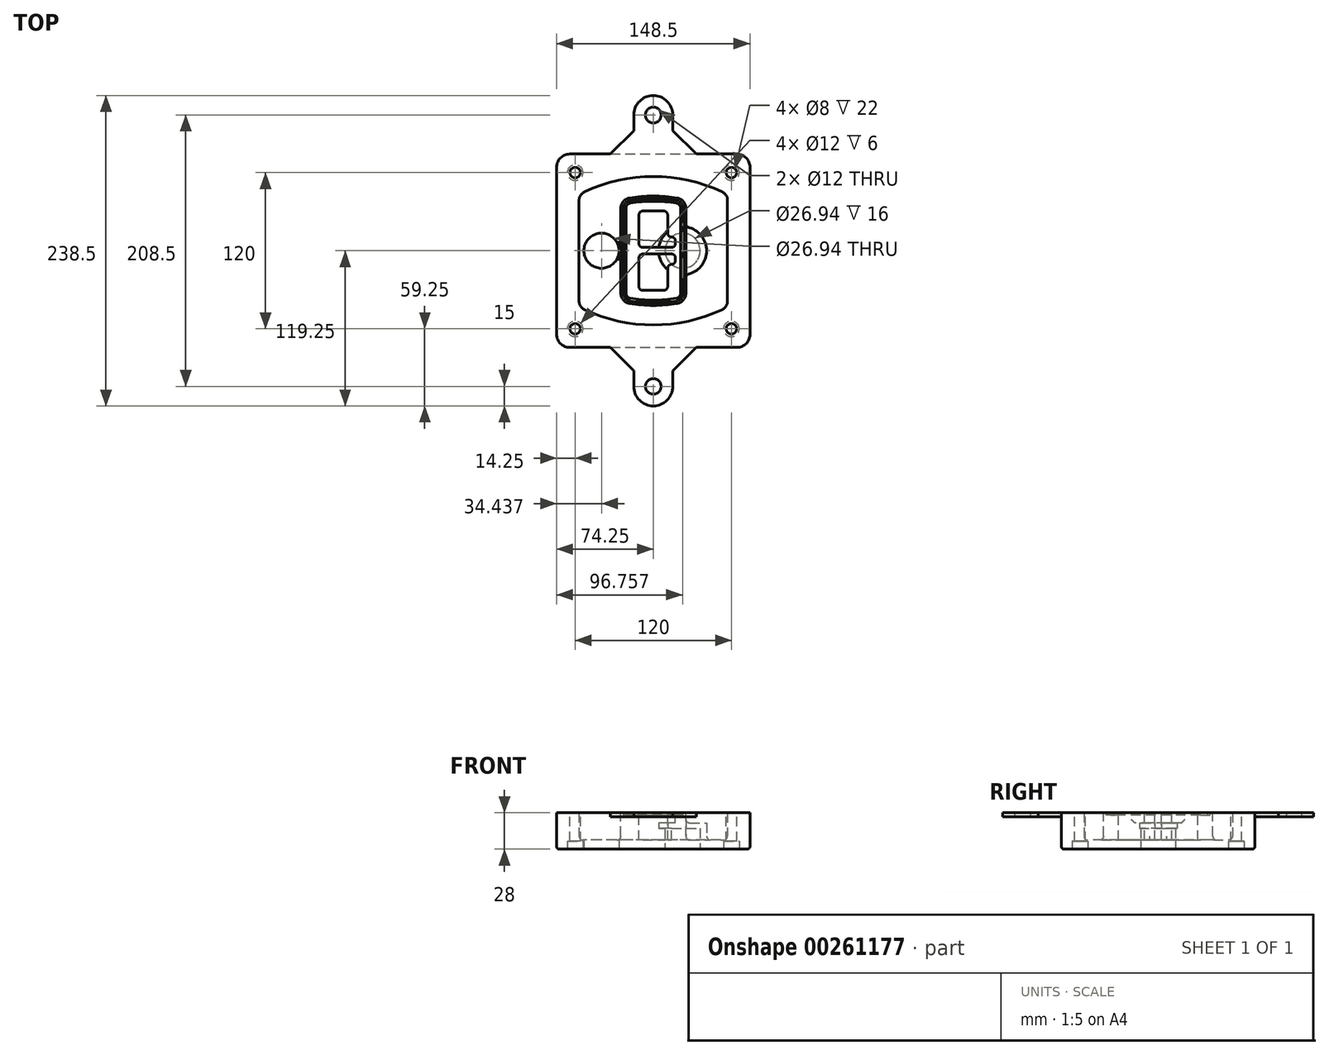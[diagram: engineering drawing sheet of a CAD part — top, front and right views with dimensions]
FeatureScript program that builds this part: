
annotation { "Feature Type Name" : "Feature", "Feature Type Description" : "" }
export const myFeature = defineFeature(function(context is Context, id is Id, definition is map)
    precondition{}
    {
        {
            var Q0;
            Q0=qCreatedBy(makeId("Top.planeOp"),FACE);
            var sketch = newSketch(context, id + "F0", { "sketchPlane" : qUnion([Q0])});
            skPoint(sketch, "E0.rect.middle", {"position": v(0, 0) * mm});
            skLineSegment(sketch, "E1.bottom", {"start": v(-64.25, -74.25) * mm, "end": v(64.25, -74.25) * mm});
            skLineSegment(sketch, "E1.top", {"start": v(-64.25, 74.25) * mm, "end": v(64.25, 74.25) * mm});
            skLineSegment(sketch, "E1.left", {"start": v(-74.25, -64.25) * mm, "end": v(-74.25, 64.25) * mm});
            skLineSegment(sketch, "E1.right", {"start": v(74.25, -64.25) * mm, "end": v(74.25, 64.25) * mm});
            skLineSegment(sketch, "E2", {"start": v(-74.25, 74.25) * mm, "end": v(74.25, -74.25) * mm, "construction": true});
            skLineSegment(sketch, "E3", {"start": v(74.25, 74.25) * mm, "end": v(-74.25, -74.25) * mm, "construction": true});
            skCircle(sketch, "E4", {"center": v(-60, 60) * mm, "radius": 4 * mm});
            skCircle(sketch, "E5", {"center": v(60, 60) * mm, "radius": 4 * mm});
            skCircle(sketch, "E6", {"center": v(60, -60) * mm, "radius": 4 * mm});
            skCircle(sketch, "E7", {"center": v(-60, -60) * mm, "radius": 4 * mm});
            skLineSegment(sketch, "E8", {"start": v(-60, 60) * mm, "end": v(60, 60) * mm, "construction": true});
            skLineSegment(sketch, "E9", {"start": v(60, 60) * mm, "end": v(60, -60) * mm, "construction": true});
            skLineSegment(sketch, "E10", {"start": v(60, -60) * mm, "end": v(-60, -60) * mm, "construction": true});
            skLineSegment(sketch, "E11", {"start": v(-60, -60) * mm, "end": v(-60, 60) * mm, "construction": true});
            skLineSegment(sketch, "E12", {"start": v(-60, 38.83) * mm, "end": v(-60, -38.83) * mm});
            skLineSegment(sketch, "E13", {"start": v(60, 38.83) * mm, "end": v(60, -38.83) * mm});
            skArc(sketch, "E14", {"start": v(54.26, 47.88) * mm, "mid": v(0, 60) * mm, "end": v(-54.26, 47.88) * mm});
            skArc(sketch, "E15", {"start": v(-54.26, -47.88) * mm, "mid": v(0, -60) * mm, "end": v(54.26, -47.88) * mm});
            skLineSegment(sketch, "E16", {"start": v(-60, 0) * mm, "end": v(60, 0) * mm, "construction": true});
            skPoint(sketch, "E17.visualSharp", {"position": v(-60, -45) * mm});
            skArc(sketch, "E17.filletArc", {"start": v(-60, -38.83) * mm, "mid": v(-58.44, -44.2) * mm, "end": v(-54.26, -47.88) * mm});
            skPoint(sketch, "E18.visualSharp", {"position": v(-60, 45) * mm});
            skArc(sketch, "E18.filletArc", {"start": v(-54.26, 47.88) * mm, "mid": v(-58.44, 44.2) * mm, "end": v(-60, 38.83) * mm});
            skPoint(sketch, "E19.visualSharp", {"position": v(60, 45) * mm});
            skArc(sketch, "E19.filletArc", {"start": v(60, 38.83) * mm, "mid": v(58.44, 44.2) * mm, "end": v(54.26, 47.88) * mm});
            skPoint(sketch, "E20.visualSharp", {"position": v(60, -45) * mm});
            skArc(sketch, "E20.filletArc", {"start": v(54.26, -47.88) * mm, "mid": v(58.44, -44.2) * mm, "end": v(60, -38.83) * mm});
            skPoint(sketch, "E21.visualSharp", {"position": v(-74.25, 74.25) * mm});
            skArc(sketch, "E21.filletArc", {"start": v(-64.25, 74.25) * mm, "mid": v(-71.32, 71.32) * mm, "end": v(-74.25, 64.25) * mm});
            skPoint(sketch, "E22.visualSharp", {"position": v(74.25, 74.25) * mm});
            skArc(sketch, "E22.filletArc", {"start": v(74.25, 64.25) * mm, "mid": v(71.32, 71.32) * mm, "end": v(64.25, 74.25) * mm});
            skPoint(sketch, "E23.visualSharp", {"position": v(74.25, -74.25) * mm});
            skArc(sketch, "E23.filletArc", {"start": v(64.25, -74.25) * mm, "mid": v(71.32, -71.32) * mm, "end": v(74.25, -64.25) * mm});
            skPoint(sketch, "E24.visualSharp", {"position": v(-74.25, -74.25) * mm});
            skArc(sketch, "E24.filletArc", {"start": v(-74.25, -64.25) * mm, "mid": v(-71.32, -71.32) * mm, "end": v(-64.25, -74.25) * mm});
            skArc(sketch, "E25.0", {"start": v(57, 38.83) * mm, "mid": v(55.9, 42.58) * mm, "end": v(52.98, 45.17) * mm});
            skLineSegment(sketch, "E25.1", {"start": v(57, 38.83) * mm, "end": v(57, -38.83) * mm});
            skArc(sketch, "E25.2", {"start": v(52.98, -45.17) * mm, "mid": v(55.9, -42.58) * mm, "end": v(57, -38.83) * mm});
            skArc(sketch, "E25.3", {"start": v(-52.98, -45.17) * mm, "mid": v(0, -57) * mm, "end": v(52.98, -45.17) * mm});
            skArc(sketch, "E25.4", {"start": v(-57, -38.83) * mm, "mid": v(-55.9, -42.58) * mm, "end": v(-52.98, -45.17) * mm});
            skArc(sketch, "E25.5", {"start": v(52.98, 45.17) * mm, "mid": v(0, 57) * mm, "end": v(-52.98, 45.17) * mm});
            skLineSegment(sketch, "E25.6", {"start": v(-57, 38.83) * mm, "end": v(-57, -38.83) * mm});
            skArc(sketch, "E25.7", {"start": v(-52.98, 45.17) * mm, "mid": v(-55.9, 42.58) * mm, "end": v(-57, 38.83) * mm});
            skArc(sketch, "E26.0", {"start": v(-55.96, 51.5) * mm, "mid": v(-61.82, 46.33) * mm, "end": v(-64, 38.83) * mm});
            skArc(sketch, "E26.1", {"start": v(55.96, 51.5) * mm, "mid": v(0, 64) * mm, "end": v(-55.96, 51.5) * mm});
            skArc(sketch, "E26.2", {"start": v(64, 38.83) * mm, "mid": v(61.82, 46.33) * mm, "end": v(55.96, 51.5) * mm});
            skLineSegment(sketch, "E26.3", {"start": v(64, 38.83) * mm, "end": v(64, -38.83) * mm});
            skArc(sketch, "E26.4", {"start": v(55.96, -51.5) * mm, "mid": v(61.82, -46.33) * mm, "end": v(64, -38.83) * mm});
            skLineSegment(sketch, "E26.5", {"start": v(-64, 38.83) * mm, "end": v(-64, -38.83) * mm});
            skArc(sketch, "E26.6", {"start": v(-55.96, -51.5) * mm, "mid": v(0, -64) * mm, "end": v(55.96, -51.5) * mm});
            skArc(sketch, "E26.7", {"start": v(-64, -38.83) * mm, "mid": v(-61.82, -46.33) * mm, "end": v(-55.96, -51.5) * mm});
            skSolve(sketch);
        }
        {
            var Q0;
            Q0=makeQuery(id+"F0.imprint","IMPRINT",FACE,{"disambiguationData":[TD([[makeQuery(id+"F0.imprint","IMPRINT",EDGE,{"derivedFrom":sQuery(id+"F0.wireOp",EDGE,"E1.bottom")}),1.0]])]});
            var Q1;
            Q1=makeQuery(id+"F0.imprint","IMPRINT",FACE,{"disambiguationData":[TD([[makeQuery(id+"F0.imprint","IMPRINT",EDGE,{"derivedFrom":sQuery(id+"F0.wireOp",EDGE,"E12")}),1.0]])]});
            var Q2;
            Q2=makeQuery(id+"F0.imprint","IMPRINT",FACE,{"disambiguationData":[TD([[makeQuery(id+"F0.imprint","IMPRINT",EDGE,{"derivedFrom":sQuery(id+"F0.wireOp",EDGE,"E25.0")}),1.0]])]});
            var Q3;
            Q3=makeQuery(id+"F0.imprint","IMPRINT",FACE,{"disambiguationData":[TD([[makeQuery(id+"F0.imprint","IMPRINT",EDGE,{"derivedFrom":sQuery(id+"F0.wireOp",EDGE,"E12")}),-1.0]])]});
            extrude(context, id + "F1", {"entities" : qUnion([Q0, Q1, Q2, Q3]), "oppositeDirection" : true, "depth" : 25 * mm});
        }
        {
            var Q0;
            Q0=makeQuery(id+"F0.imprint","IMPRINT",FACE,{"disambiguationData":[TD([[makeQuery(id+"F0.imprint","IMPRINT",EDGE,{"derivedFrom":sQuery(id+"F0.wireOp",EDGE,"E12")}),1.0]])]});
            extrude(context, id + "F2", {"entities" : qUnion([Q0]), "operationType" : NewBodyOperationType.ADD, "depth" : 3 * mm});
        }
        {
            var Q0;
            Q0=makeQuery(id+"F0.imprint","IMPRINT",FACE,{"disambiguationData":[TD([[makeQuery(id+"F0.imprint","IMPRINT",EDGE,{"derivedFrom":sQuery(id+"F0.wireOp",EDGE,"E25.0")}),1.0]])]});
            extrude(context, id + "F3", {"entities" : qUnion([Q0]), "operationType" : NewBodyOperationType.REMOVE, "oppositeDirection" : true, "depth" : 18 * mm});
        }
        {
            var Q0;
            Q0=makeQuery(id+"F2.opExtrude","CAP_FACE",FACE,{"disambiguationData":[OSD([sQuery(id+"F0.wireOp",EDGE,"E12"),sQuery(id+"F0.wireOp",EDGE,"E13"),sQuery(id+"F0.wireOp",EDGE,"E14"),sQuery(id+"F0.wireOp",EDGE,"E15"),sQuery(id+"F0.wireOp",EDGE,"E17.filletArc"),sQuery(id+"F0.wireOp",EDGE,"E18.filletArc"),sQuery(id+"F0.wireOp",EDGE,"E19.filletArc"),sQuery(id+"F0.wireOp",EDGE,"E20.filletArc"),sQuery(id+"F0.wireOp",EDGE,"E25.0"),sQuery(id+"F0.wireOp",EDGE,"E25.1"),sQuery(id+"F0.wireOp",EDGE,"E25.2"),sQuery(id+"F0.wireOp",EDGE,"E25.3"),sQuery(id+"F0.wireOp",EDGE,"E25.4"),sQuery(id+"F0.wireOp",EDGE,"E25.5"),sQuery(id+"F0.wireOp",EDGE,"E25.6"),sQuery(id+"F0.wireOp",EDGE,"E25.7")])],"isStart":false});
            var sketch = newSketch(context, id + "F4", { "sketchPlane" : qUnion([Q0])});
            skArc(sketch, "E27.0", {"start": v(-18.34, -40.45) * mm, "mid": v(0, -42) * mm, "end": v(18.34, -40.45) * mm});
            skArc(sketch, "E28.0", {"start": v(18.34, 40.45) * mm, "mid": v(0, 42) * mm, "end": v(-18.34, 40.45) * mm});
            skLineSegment(sketch, "E29", {"start": v(-25, 32.57) * mm, "end": v(-25, -32.57) * mm});
            skLineSegment(sketch, "E30", {"start": v(25, 32.57) * mm, "end": v(25, -32.57) * mm});
            skLineSegment(sketch, "E31", {"start": v(-25, 39.1) * mm, "end": v(25, 39.1) * mm, "construction": true});
            skLineSegment(sketch, "E32", {"start": v(-25, -39.1) * mm, "end": v(25, -39.1) * mm, "construction": true});
            skPoint(sketch, "E33.visualSharp", {"position": v(-25, 39.1) * mm});
            skArc(sketch, "E33.filletArc", {"start": v(-18.34, 40.45) * mm, "mid": v(-23.11, 37.73) * mm, "end": v(-25, 32.57) * mm});
            skPoint(sketch, "E34.visualSharp", {"position": v(25, 39.1) * mm});
            skArc(sketch, "E34.filletArc", {"start": v(25, 32.57) * mm, "mid": v(23.11, 37.73) * mm, "end": v(18.34, 40.45) * mm});
            skPoint(sketch, "E35.visualSharp", {"position": v(25, -39.1) * mm});
            skArc(sketch, "E35.filletArc", {"start": v(18.34, -40.45) * mm, "mid": v(23.11, -37.73) * mm, "end": v(25, -32.57) * mm});
            skPoint(sketch, "E36.visualSharp", {"position": v(-25, -39.1) * mm});
            skArc(sketch, "E36.filletArc", {"start": v(-25, -32.57) * mm, "mid": v(-23.11, -37.73) * mm, "end": v(-18.34, -40.45) * mm});
            skArc(sketch, "E37.0", {"start": v(52.98, 45.17) * mm, "mid": v(0, 57) * mm, "end": v(-52.98, 45.17) * mm});
            skArc(sketch, "E37.1", {"start": v(-52.98, 45.17) * mm, "mid": v(-55.9, 42.58) * mm, "end": v(-57, 38.83) * mm});
            skLineSegment(sketch, "E37.2", {"start": v(-57, 38.83) * mm, "end": v(-57, -38.83) * mm});
            skArc(sketch, "E37.3", {"start": v(-57, -38.83) * mm, "mid": v(-55.9, -42.58) * mm, "end": v(-52.98, -45.17) * mm});
            skArc(sketch, "E37.4", {"start": v(-52.98, -45.17) * mm, "mid": v(0, -57) * mm, "end": v(52.98, -45.17) * mm});
            skArc(sketch, "E37.5", {"start": v(52.98, -45.17) * mm, "mid": v(55.9, -42.58) * mm, "end": v(57, -38.83) * mm});
            skLineSegment(sketch, "E37.6", {"start": v(57, 38.83) * mm, "end": v(57, -38.83) * mm});
            skArc(sketch, "E37.7", {"start": v(57, 38.83) * mm, "mid": v(55.9, 42.58) * mm, "end": v(52.98, 45.17) * mm});
            skLineSegment(sketch, "E38.0", {"start": v(23, 32.57) * mm, "end": v(23, -32.57) * mm});
            skArc(sketch, "E38.1", {"start": v(18, -38.48) * mm, "mid": v(21.58, -36.44) * mm, "end": v(23, -32.57) * mm});
            skArc(sketch, "E38.2", {"start": v(-18, -38.48) * mm, "mid": v(0, -40) * mm, "end": v(18, -38.48) * mm});
            skArc(sketch, "E38.3", {"start": v(-23, -32.57) * mm, "mid": v(-21.58, -36.44) * mm, "end": v(-18, -38.48) * mm});
            skLineSegment(sketch, "E38.4", {"start": v(-23, 32.57) * mm, "end": v(-23, -32.57) * mm});
            skArc(sketch, "E38.5", {"start": v(23, 32.57) * mm, "mid": v(21.58, 36.44) * mm, "end": v(18, 38.48) * mm});
            skArc(sketch, "E38.6", {"start": v(-18, 38.48) * mm, "mid": v(-21.58, 36.44) * mm, "end": v(-23, 32.57) * mm});
            skArc(sketch, "E38.7", {"start": v(18, 38.48) * mm, "mid": v(0, 40) * mm, "end": v(-18, 38.48) * mm});
            skArc(sketch, "E39.0", {"start": v(21, 32.57) * mm, "mid": v(20.06, 35.15) * mm, "end": v(17.67, 36.5) * mm});
            skLineSegment(sketch, "E39.1", {"start": v(21, 32.57) * mm, "end": v(21, -32.57) * mm});
            skArc(sketch, "E39.2", {"start": v(17.67, -36.5) * mm, "mid": v(20.06, -35.15) * mm, "end": v(21, -32.57) * mm});
            skArc(sketch, "E39.3", {"start": v(-17.67, -36.5) * mm, "mid": v(0, -38) * mm, "end": v(17.67, -36.5) * mm});
            skArc(sketch, "E39.4", {"start": v(-21, -32.57) * mm, "mid": v(-20.06, -35.15) * mm, "end": v(-17.67, -36.5) * mm});
            skArc(sketch, "E39.5", {"start": v(17.67, 36.5) * mm, "mid": v(0, 38) * mm, "end": v(-17.67, 36.5) * mm});
            skLineSegment(sketch, "E39.6", {"start": v(-21, 32.57) * mm, "end": v(-21, -32.57) * mm});
            skArc(sketch, "E39.7", {"start": v(-17.67, 36.5) * mm, "mid": v(-20.06, 35.15) * mm, "end": v(-21, 32.57) * mm});
            skLineSegment(sketch, "E40", {"start": v(-25, 0) * mm, "end": v(25, 0) * mm, "construction": true});
            skLineSegment(sketch, "E41", {"start": v(-11, 5.5) * mm, "end": v(-11, 27.5) * mm});
            skLineSegment(sketch, "E42", {"start": v(-8, 30.5) * mm, "end": v(8, 30.5) * mm});
            skLineSegment(sketch, "E43", {"start": v(11, 27.5) * mm, "end": v(11, 13.5) * mm});
            skLineSegment(sketch, "E44", {"start": v(14, 10.5) * mm, "end": v(14, 10.5) * mm});
            skLineSegment(sketch, "E45", {"start": v(17, 7.5) * mm, "end": v(17, 5.5) * mm});
            skLineSegment(sketch, "E46", {"start": v(14, 2.5) * mm, "end": v(-8, 2.5) * mm});
            skPoint(sketch, "E47.visualSharp", {"position": v(-11, 30.5) * mm});
            skArc(sketch, "E47.filletArc", {"start": v(-8, 30.5) * mm, "mid": v(-10.12, 29.62) * mm, "end": v(-11, 27.5) * mm});
            skPoint(sketch, "E48.visualSharp", {"position": v(11, 30.5) * mm});
            skArc(sketch, "E48.filletArc", {"start": v(11, 27.5) * mm, "mid": v(10.12, 29.62) * mm, "end": v(8, 30.5) * mm});
            skPoint(sketch, "E49.visualSharp", {"position": v(11, 10.5) * mm});
            skArc(sketch, "E49.filletArc", {"start": v(11, 13.5) * mm, "mid": v(11.88, 11.38) * mm, "end": v(14, 10.5) * mm});
            skPoint(sketch, "E50.visualSharp", {"position": v(17, 10.5) * mm});
            skArc(sketch, "E50.filletArc", {"start": v(17, 7.5) * mm, "mid": v(16.12, 9.62) * mm, "end": v(14, 10.5) * mm});
            skPoint(sketch, "E51.visualSharp", {"position": v(17, 2.5) * mm});
            skArc(sketch, "E51.filletArc", {"start": v(14, 2.5) * mm, "mid": v(16.12, 3.38) * mm, "end": v(17, 5.5) * mm});
            skPoint(sketch, "E52.visualSharp", {"position": v(-11, 2.5) * mm});
            skArc(sketch, "E52.filletArc", {"start": v(-11, 5.5) * mm, "mid": v(-10.12, 3.38) * mm, "end": v(-8, 2.5) * mm});
            skLineSegment(sketch, "E53.0.MirrorCS", {"start": v(14, -2.5) * mm, "end": v(-8, -2.5) * mm});
            skArc(sketch, "E54.0.MirrorCS", {"start": v(-11, -5.5) * mm, "mid": v(-10.12, -3.38) * mm, "end": v(-8, -2.5) * mm});
            skLineSegment(sketch, "E55.0.MirrorCS", {"start": v(-11, -5.5) * mm, "end": v(-11, -27.5) * mm});
            skArc(sketch, "E56.0.MirrorCS", {"start": v(-8, -30.5) * mm, "mid": v(-10.12, -29.62) * mm, "end": v(-11, -27.5) * mm});
            skLineSegment(sketch, "E57.0.MirrorCS", {"start": v(-8, -30.5) * mm, "end": v(8, -30.5) * mm});
            skArc(sketch, "E58.0.MirrorCS", {"start": v(11, -27.5) * mm, "mid": v(10.12, -29.62) * mm, "end": v(8, -30.5) * mm});
            skLineSegment(sketch, "E59.0.MirrorCS", {"start": v(11, -27.5) * mm, "end": v(11, -13.5) * mm});
            skArc(sketch, "E60.0.MirrorCS", {"start": v(11, -13.5) * mm, "mid": v(11.88, -11.38) * mm, "end": v(14, -10.5) * mm});
            skArc(sketch, "E61.0.MirrorCS", {"start": v(17, -7.5) * mm, "mid": v(16.12, -9.62) * mm, "end": v(14, -10.5) * mm});
            skLineSegment(sketch, "E62.0.MirrorCS", {"start": v(17, -7.5) * mm, "end": v(17, -5.5) * mm});
            skArc(sketch, "E63.0.MirrorCS", {"start": v(14, -2.5) * mm, "mid": v(16.12, -3.38) * mm, "end": v(17, -5.5) * mm});
            skSolve(sketch);
        }
        {
            var Q0;
            Q0=makeQuery(id+"F4.imprint","IMPRINT",FACE,{"disambiguationData":[TD([[makeQuery(id+"F4.imprint","IMPRINT",EDGE,{"derivedFrom":sQuery(id+"F4.wireOp",EDGE,"E27.0")}),1.0]])]});
            var Q1;
            Q1=makeQuery(id+"F4.imprint","IMPRINT",FACE,{"disambiguationData":[TD([[makeQuery(id+"F4.imprint","IMPRINT",EDGE,{"derivedFrom":sQuery(id+"F4.wireOp",EDGE,"E38.0")}),-1.0]])]});
            var Q2;
            Q2=makeQuery(id+"F4.imprint","IMPRINT",FACE,{"disambiguationData":[TD([[makeQuery(id+"F4.imprint","IMPRINT",EDGE,{"derivedFrom":sQuery(id+"F4.wireOp",EDGE,"E39.0")}),1.0]])]});
            extrude(context, id + "F5", {"entities" : qUnion([Q0, Q1, Q2]), "operationType" : NewBodyOperationType.ADD, "endBound" : BoundingType.UP_TO_NEXT, "oppositeDirection" : true, "depth" : 25 * mm});
        }
        {
            var Q0;
            Q0=makeQuery(id+"F4.imprint","IMPRINT",FACE,{"disambiguationData":[TD([[makeQuery(id+"F4.imprint","IMPRINT",EDGE,{"derivedFrom":sQuery(id+"F4.wireOp",EDGE,"E38.0")}),-1.0]])]});
            extrude(context, id + "F6", {"entities" : qUnion([Q0]), "operationType" : NewBodyOperationType.REMOVE, "oppositeDirection" : true, "depth" : 2 * mm});
        }
        {
            var Q0;
            Q0=makeQuery(id+"F1.opExtrude","CAP_FACE",FACE,{"disambiguationData":[OSD([sQuery(id+"F0.wireOp",EDGE,"E1.bottom"),sQuery(id+"F0.wireOp",EDGE,"E1.top"),sQuery(id+"F0.wireOp",EDGE,"E1.left"),sQuery(id+"F0.wireOp",EDGE,"E1.right"),sQuery(id+"F0.wireOp",EDGE,"E4"),sQuery(id+"F0.wireOp",EDGE,"E5"),sQuery(id+"F0.wireOp",EDGE,"E6"),sQuery(id+"F0.wireOp",EDGE,"E7"),sQuery(id+"F0.wireOp",EDGE,"E21.filletArc"),sQuery(id+"F0.wireOp",EDGE,"E22.filletArc"),sQuery(id+"F0.wireOp",EDGE,"E23.filletArc"),sQuery(id+"F0.wireOp",EDGE,"E24.filletArc")])],"isStart":false});
            var sketch = newSketch(context, id + "F7", { "sketchPlane" : qUnion([Q0])});
            skCircle(sketch, "E64", {"center": v(22.5, 0) * mm, "radius": 13.47 * mm});
            skCircle(sketch, "E65", {"center": v(-39.81, 0) * mm, "radius": 13.47 * mm});
            skLineSegment(sketch, "E66", {"start": v(74.25, 0) * mm, "end": v(-74.25, 0) * mm});
            skCircle(sketch, "E67", {"center": v(22.5, 0) * mm, "radius": 18.47 * mm});
            skCircle(sketch, "E68", {"center": v(60, -60) * mm, "radius": 6 * mm});
            skCircle(sketch, "E69", {"center": v(-60, -60) * mm, "radius": 6 * mm});
            skCircle(sketch, "E70", {"center": v(-60, 60) * mm, "radius": 6 * mm});
            skCircle(sketch, "E71", {"center": v(60, 60) * mm, "radius": 6 * mm});
            skSolve(sketch);
        }
        {
            var Q0;
            {var subQ1=sQuery(id+"F7.wireOp",EDGE,"E66");var subQ4=sQuery(id+"F7.wireOp",EDGE,"E64");var subQ6=makeQuery(id+"F7.imprint","INTERSECT",VERTEX,{"disambiguationData":[OD(0.0)],"derivedFrom":[subQ4,subQ1]});Q0=makeQuery(id+"F7.imprint","IMPRINT",FACE,{"disambiguationData":[TD([[makeQuery(id+"F7.imprint","IMPRINT",EDGE,{"disambiguationData":[TD([[subQ6,-1.0]])],"derivedFrom":subQ4}),-1.0]])]});}
            var Q1;
            {var subQ0=sQuery(id+"F7.wireOp",EDGE,"E66");var subQ1=sQuery(id+"F7.wireOp",EDGE,"E64");var subQ3=makeQuery(id+"F7.imprint","INTERSECT",VERTEX,{"disambiguationData":[OD(0.0)],"derivedFrom":[subQ1,subQ0]});Q1=makeQuery(id+"F7.imprint","IMPRINT",FACE,{"disambiguationData":[TD([[makeQuery(id+"F7.imprint","IMPRINT",EDGE,{"disambiguationData":[TD([[subQ3,-1.0]])],"derivedFrom":subQ1}),1.0]])]});}
            var Q2;
            {var subQ0=sQuery(id+"F7.wireOp",EDGE,"E66");var subQ1=sQuery(id+"F7.wireOp",EDGE,"E64");var subQ3=makeQuery(id+"F7.imprint","INTERSECT",VERTEX,{"disambiguationData":[OD(0.0)],"derivedFrom":[subQ1,subQ0]});Q2=makeQuery(id+"F7.imprint","IMPRINT",FACE,{"disambiguationData":[TD([[makeQuery(id+"F7.imprint","IMPRINT",EDGE,{"disambiguationData":[TD([[subQ3,1.0]])],"derivedFrom":subQ1}),1.0]])]});}
            var Q3;
            {var subQ1=sQuery(id+"F7.wireOp",EDGE,"E66");var subQ4=sQuery(id+"F7.wireOp",EDGE,"E64");var subQ6=makeQuery(id+"F7.imprint","INTERSECT",VERTEX,{"disambiguationData":[OD(0.0)],"derivedFrom":[subQ4,subQ1]});Q3=makeQuery(id+"F7.imprint","IMPRINT",FACE,{"disambiguationData":[TD([[makeQuery(id+"F7.imprint","IMPRINT",EDGE,{"disambiguationData":[TD([[subQ6,1.0]])],"derivedFrom":subQ4}),-1.0]])]});}
            extrude(context, id + "F8", {"entities" : qUnion([Q0, Q1, Q2, Q3]), "operationType" : NewBodyOperationType.ADD, "oppositeDirection" : true, "depth" : 20 * mm});
        }
        {
            var Q0;
            {var subQ0=sQuery(id+"F7.wireOp",EDGE,"E66");var subQ1=sQuery(id+"F7.wireOp",EDGE,"E64");var subQ3=makeQuery(id+"F7.imprint","INTERSECT",VERTEX,{"disambiguationData":[OD(0.0)],"derivedFrom":[subQ1,subQ0]});Q0=makeQuery(id+"F7.imprint","IMPRINT",FACE,{"disambiguationData":[TD([[makeQuery(id+"F7.imprint","IMPRINT",EDGE,{"disambiguationData":[TD([[subQ3,-1.0]])],"derivedFrom":subQ1}),1.0]])]});}
            var Q1;
            {var subQ0=sQuery(id+"F7.wireOp",EDGE,"E66");var subQ1=sQuery(id+"F7.wireOp",EDGE,"E64");var subQ3=makeQuery(id+"F7.imprint","INTERSECT",VERTEX,{"disambiguationData":[OD(0.0)],"derivedFrom":[subQ1,subQ0]});Q1=makeQuery(id+"F7.imprint","IMPRINT",FACE,{"disambiguationData":[TD([[makeQuery(id+"F7.imprint","IMPRINT",EDGE,{"disambiguationData":[TD([[subQ3,1.0]])],"derivedFrom":subQ1}),1.0]])]});}
            extrude(context, id + "F9", {"entities" : qUnion([Q0, Q1]), "operationType" : NewBodyOperationType.REMOVE, "oppositeDirection" : true, "depth" : 16 * mm});
        }
        {
            var Q0;
            {var subQ0=sQuery(id+"F7.wireOp",EDGE,"E66");var subQ1=sQuery(id+"F7.wireOp",EDGE,"E65");var subQ3=makeQuery(id+"F7.imprint","INTERSECT",VERTEX,{"disambiguationData":[OD(0.0)],"derivedFrom":[subQ1,subQ0]});Q0=makeQuery(id+"F7.imprint","IMPRINT",FACE,{"disambiguationData":[TD([[makeQuery(id+"F7.imprint","IMPRINT",EDGE,{"disambiguationData":[TD([[subQ3,-1.0]])],"derivedFrom":subQ1}),1.0]])]});}
            var Q1;
            {var subQ0=sQuery(id+"F7.wireOp",EDGE,"E66");var subQ1=sQuery(id+"F7.wireOp",EDGE,"E65");var subQ3=makeQuery(id+"F7.imprint","INTERSECT",VERTEX,{"disambiguationData":[OD(0.0)],"derivedFrom":[subQ1,subQ0]});Q1=makeQuery(id+"F7.imprint","IMPRINT",FACE,{"disambiguationData":[TD([[makeQuery(id+"F7.imprint","IMPRINT",EDGE,{"disambiguationData":[TD([[subQ3,1.0]])],"derivedFrom":subQ1}),1.0]])]});}
            extrude(context, id + "F10", {"entities" : qUnion([Q0, Q1]), "operationType" : NewBodyOperationType.REMOVE, "oppositeDirection" : true, "depth" : 25 * mm});
        }
        {
            var Q0;
            Q0=makeQuery(id+"F7.imprint","IMPRINT",FACE,{"disambiguationData":[TD([[makeQuery(id+"F7.imprint","IMPRINT",EDGE,{"derivedFrom":sQuery(id+"F7.wireOp",EDGE,"E68")}),1.0]])]});
            var Q1;
            Q1=makeQuery(id+"F7.imprint","IMPRINT",FACE,{"disambiguationData":[TD([[makeQuery(id+"F7.imprint","IMPRINT",EDGE,{"derivedFrom":makeQuery(id+"F1.opExtrude","CAP_EDGE",EDGE,{"disambiguationData":[OSD([sQuery(id+"F0.wireOp",EDGE,"E5")])],"isStart":false})}),-1.0]])]});
            var Q2;
            Q2=makeQuery(id+"F7.imprint","IMPRINT",FACE,{"disambiguationData":[TD([[makeQuery(id+"F7.imprint","IMPRINT",EDGE,{"derivedFrom":sQuery(id+"F7.wireOp",EDGE,"E69")}),1.0]])]});
            var Q3;
            Q3=makeQuery(id+"F7.imprint","IMPRINT",FACE,{"disambiguationData":[TD([[makeQuery(id+"F7.imprint","IMPRINT",EDGE,{"derivedFrom":makeQuery(id+"F1.opExtrude","CAP_EDGE",EDGE,{"disambiguationData":[OSD([sQuery(id+"F0.wireOp",EDGE,"E4")])],"isStart":false})}),-1.0]])]});
            var Q4;
            Q4=makeQuery(id+"F7.imprint","IMPRINT",FACE,{"disambiguationData":[TD([[makeQuery(id+"F7.imprint","IMPRINT",EDGE,{"derivedFrom":sQuery(id+"F7.wireOp",EDGE,"E70")}),1.0]])]});
            var Q5;
            Q5=makeQuery(id+"F7.imprint","IMPRINT",FACE,{"disambiguationData":[TD([[makeQuery(id+"F7.imprint","IMPRINT",EDGE,{"derivedFrom":makeQuery(id+"F1.opExtrude","CAP_EDGE",EDGE,{"disambiguationData":[OSD([sQuery(id+"F0.wireOp",EDGE,"E7")])],"isStart":false})}),-1.0]])]});
            var Q6;
            Q6=makeQuery(id+"F7.imprint","IMPRINT",FACE,{"disambiguationData":[TD([[makeQuery(id+"F7.imprint","IMPRINT",EDGE,{"derivedFrom":sQuery(id+"F7.wireOp",EDGE,"E71")}),1.0]])]});
            var Q7;
            Q7=makeQuery(id+"F7.imprint","IMPRINT",FACE,{"disambiguationData":[TD([[makeQuery(id+"F7.imprint","IMPRINT",EDGE,{"derivedFrom":makeQuery(id+"F1.opExtrude","CAP_EDGE",EDGE,{"disambiguationData":[OSD([sQuery(id+"F0.wireOp",EDGE,"E6")])],"isStart":false})}),-1.0]])]});
            extrude(context, id + "F11", {"entities" : qUnion([Q0, Q1, Q2, Q3, Q4, Q5, Q6, Q7]), "operationType" : NewBodyOperationType.REMOVE, "oppositeDirection" : true, "depth" : 6 * mm});
        }
        {
            var Q0;
            Q0=makeQuery(id+"F9.boolean.opBoolean","COPY",FACE,{"derivedFrom":makeQuery(id+"F9.opExtrude","CAP_FACE",FACE,{"disambiguationData":[OSD([sQuery(id+"F7.wireOp",EDGE,"E64")])],"isStart":false})});
            var sketch = newSketch(context, id + "F12", { "sketchPlane" : qUnion([Q0])});
            skArc(sketch, "E72.0", {"start": v(11, 14.45) * mm, "mid": v(6.45, 9.13) * mm, "end": v(4.2, 2.5) * mm});
            skArc(sketch, "E72.1", {"start": v(4.2, -2.5) * mm, "mid": v(6.45, -9.13) * mm, "end": v(11, -14.45) * mm});
            skLineSegment(sketch, "E73", {"start": v(4.2, -2.5) * mm, "end": v(14, -2.5) * mm});
            skLineSegment(sketch, "E74.0", {"start": v(14, 2.5) * mm, "end": v(4.2, 2.5) * mm});
            skArc(sketch, "E74.1", {"start": v(14, 2.5) * mm, "mid": v(16.12, 3.38) * mm, "end": v(17, 5.5) * mm});
            skLineSegment(sketch, "E74.2", {"start": v(17, 7.5) * mm, "end": v(17, 5.5) * mm});
            skArc(sketch, "E74.3", {"start": v(17, 7.5) * mm, "mid": v(16.12, 9.62) * mm, "end": v(14, 10.5) * mm});
            skArc(sketch, "E74.4", {"start": v(11, 13.5) * mm, "mid": v(11.88, 11.38) * mm, "end": v(14, 10.5) * mm});
            skLineSegment(sketch, "E74.5", {"start": v(11, 14.45) * mm, "end": v(11, 13.5) * mm});
            skLineSegment(sketch, "E74.7", {"start": v(14, -2.5) * mm, "end": v(4.2, -2.5) * mm});
            skArc(sketch, "E74.8", {"start": v(14, -2.5) * mm, "mid": v(16.12, -3.38) * mm, "end": v(17, -5.5) * mm});
            skLineSegment(sketch, "E74.9", {"start": v(17, -7.5) * mm, "end": v(17, -5.5) * mm});
            skArc(sketch, "E74.10", {"start": v(17, -7.5) * mm, "mid": v(16.12, -9.62) * mm, "end": v(14, -10.5) * mm});
            skArc(sketch, "E74.11", {"start": v(11, -13.5) * mm, "mid": v(11.88, -11.38) * mm, "end": v(14, -10.5) * mm});
            skLineSegment(sketch, "E74.12", {"start": v(11, -14.45) * mm, "end": v(11, -13.5) * mm});
            skPoint(sketch, "E75.orphan", {"position": v(11, -27.5) * mm});
            skPoint(sketch, "E76.orphan", {"position": v(-8, -2.5) * mm});
            skPoint(sketch, "E77.orphan", {"position": v(-8, 2.5) * mm});
            skPoint(sketch, "E78.orphan", {"position": v(11, 27.5) * mm});
            skSolve(sketch);
        }
        {
            var Q0;
            {var subQ7=sQuery(id+"F12.wireOp",EDGE,"E72.0");var subQ14=sQuery(id+"F12.wireOp",EDGE,"E72.1");var subQ16=sQuery(id+"F12.wireOp",EDGE,"E74.1");var subQ18=sQuery(id+"F12.wireOp",EDGE,"E74.8");Q0=qUnion([makeQuery(id+"F12.imprint","IMPRINT",FACE,{"disambiguationData":[TD([[makeQuery(id+"F12.imprint","IMPRINT",EDGE,{"derivedFrom":subQ7}),1.0]])]}),makeQuery(id+"F12.imprint","IMPRINT",FACE,{"disambiguationData":[TD([[makeQuery(id+"F12.imprint","IMPRINT",EDGE,{"derivedFrom":subQ14}),1.0]])]}),makeQuery(id+"F12.imprint","IMPRINT",FACE,{"disambiguationData":[TD([[makeQuery(id+"F12.imprint","IMPRINT",EDGE,{"derivedFrom":subQ16}),1.0]])]}),makeQuery(id+"F12.imprint","IMPRINT",FACE,{"disambiguationData":[TD([[makeQuery(id+"F12.imprint","IMPRINT",EDGE,{"derivedFrom":subQ18}),-1.0]])]})]);}
            var Q1;
            Q1=makeQuery(id+"F5.boolean.opBoolean","SPLIT",FACE,{"disambiguationData":[TD([makeQuery(id+"F5.opExtrude","SWEPT_FACE",FACE,{"disambiguationData":[OSD([sQuery(id+"F4.wireOp",EDGE,"E41")])]})])],"derivedFrom":makeQuery(id+"F3.boolean.opBoolean","COPY",FACE,{"derivedFrom":makeQuery(id+"F3.opExtrude","CAP_FACE",FACE,{"disambiguationData":[OSD([sQuery(id+"F0.wireOp",EDGE,"E25.0"),sQuery(id+"F0.wireOp",EDGE,"E25.1"),sQuery(id+"F0.wireOp",EDGE,"E25.2"),sQuery(id+"F0.wireOp",EDGE,"E25.3"),sQuery(id+"F0.wireOp",EDGE,"E25.4"),sQuery(id+"F0.wireOp",EDGE,"E25.5"),sQuery(id+"F0.wireOp",EDGE,"E25.6"),sQuery(id+"F0.wireOp",EDGE,"E25.7")])],"isStart":false})})});
            extrude(context, id + "F13", {"entities" : qUnion([Q0]), "operationType" : NewBodyOperationType.REMOVE, "endBound" : BoundingType.UP_TO_SURFACE, "endBoundEntityFace" : qUnion([Q1]), "depth" : 25 * mm});
        }
        {
            var Q0;
            Q0=makeQuery(id+"F3.boolean.opBoolean","COPY",EDGE,{"derivedFrom":makeQuery(id+"F3.opExtrude","CAP_EDGE",EDGE,{"disambiguationData":[OSD([sQuery(id+"F0.wireOp",EDGE,"E25.6")])],"isStart":false})});
            var Q1;
            Q1=makeQuery(id+"F8.boolean.opBoolean","INTERSECT",EDGE,{"derivedFrom":[makeQuery(id+"F5.opExtrude","SWEPT_FACE",FACE,{"disambiguationData":[OSD([sQuery(id+"F4.wireOp",EDGE,"E30")])]}),makeQuery(id+"F8.opExtrude","CAP_FACE",FACE,{"disambiguationData":[OSD([sQuery(id+"F7.wireOp",EDGE,"E67")])],"isStart":false})]});
            var Q2;
            Q2=makeQuery(id+"F8.boolean.opBoolean","INTERSECT",EDGE,{"disambiguationData":[OD(1.0)],"derivedFrom":[makeQuery(id+"F5.opExtrude","SWEPT_FACE",FACE,{"disambiguationData":[OSD([sQuery(id+"F4.wireOp",EDGE,"E30")])]}),makeQuery(id+"F8.opExtrude","SWEPT_FACE",FACE,{"disambiguationData":[OSD([sQuery(id+"F7.wireOp",EDGE,"E67")])]})]});
            var Q3;
            {var subQ0=sQuery(id+"F4.wireOp",EDGE,"E30");Q3=makeQuery(id+"F8.boolean.opBoolean","SPLIT",EDGE,{"disambiguationData":[TD([makeQuery(id+"F5.opExtrude","SWEPT_FACE",FACE,{"disambiguationData":[OSD([sQuery(id+"F4.wireOp",EDGE,"E35.filletArc")])]})])],"derivedFrom":makeQuery(id+"F5.opExtrude","CAP_EDGE",EDGE,{"disambiguationData":[OSD([subQ0])],"isStart":false})});}
            var Q4;
            {var subQ0=sQuery(id+"F0.wireOp",EDGE,"E25.7");var subQ1=sQuery(id+"F0.wireOp",EDGE,"E25.1");var subQ2=sQuery(id+"F0.wireOp",EDGE,"E25.6");var subQ3=sQuery(id+"F0.wireOp",EDGE,"E25.5");var subQ4=sQuery(id+"F0.wireOp",EDGE,"E25.4");var subQ5=sQuery(id+"F0.wireOp",EDGE,"E25.0");var subQ6=sQuery(id+"F0.wireOp",EDGE,"E25.2");var subQ7=sQuery(id+"F0.wireOp",EDGE,"E25.3");Q4=makeQuery(id+"F8.boolean.opBoolean","INTERSECT",EDGE,{"derivedFrom":[makeQuery(id+"F5.boolean.opBoolean","SPLIT",FACE,{"disambiguationData":[TD([makeQuery(id+"F2.opExtrude","SWEPT_FACE",FACE,{"disambiguationData":[OSD([subQ5])]})])],"derivedFrom":makeQuery(id+"F3.boolean.opBoolean","COPY",FACE,{"derivedFrom":makeQuery(id+"F3.opExtrude","CAP_FACE",FACE,{"disambiguationData":[OSD([subQ5,subQ1,subQ6,subQ7,subQ4,subQ3,subQ2,subQ0])],"isStart":false})})}),makeQuery(id+"F8.opExtrude","SWEPT_FACE",FACE,{"disambiguationData":[OSD([sQuery(id+"F7.wireOp",EDGE,"E67")])]})]});}
            var Q5;
            Q5=makeQuery(id+"F8.boolean.opBoolean","INTERSECT",EDGE,{"disambiguationData":[OD(0.0)],"derivedFrom":[makeQuery(id+"F5.opExtrude","SWEPT_FACE",FACE,{"disambiguationData":[OSD([sQuery(id+"F4.wireOp",EDGE,"E30")])]}),makeQuery(id+"F8.opExtrude","SWEPT_FACE",FACE,{"disambiguationData":[OSD([sQuery(id+"F7.wireOp",EDGE,"E67")])]})]});
            fillet(context, id + "F14", {"entities" : qUnion([Q0, Q1, Q2, Q3, Q4, Q5]), "radius" : 3 * mm, "tangentPropagation" : true, "allowEdgeOverflow" : false});
        }
        {
            var Q0;
            Q0=makeQuery(id+"F1.opExtrude","CAP_EDGE",EDGE,{"disambiguationData":[OSD([sQuery(id+"F0.wireOp",EDGE,"E1.bottom")])],"isStart":false});
            fillet(context, id + "F15", {"entities" : qUnion([Q0]), "radius" : 2 * mm, "tangentPropagation" : true, "allowEdgeOverflow" : false});
        }
        {
            var Q0;
            {var subQ0=sQuery(id+"F0.wireOp",EDGE,"E22.filletArc");var subQ1=sQuery(id+"F0.wireOp",EDGE,"E7");var subQ2=sQuery(id+"F0.wireOp",EDGE,"E6");var subQ3=sQuery(id+"F0.wireOp",EDGE,"E5");var subQ4=sQuery(id+"F0.wireOp",EDGE,"E4");var subQ5=sQuery(id+"F0.wireOp",EDGE,"E1.bottom");var subQ6=sQuery(id+"F0.wireOp",EDGE,"E21.filletArc");var subQ7=sQuery(id+"F0.wireOp",EDGE,"E1.top");var subQ8=sQuery(id+"F0.wireOp",EDGE,"E1.left");var subQ9=sQuery(id+"F0.wireOp",EDGE,"E1.right");var subQ10=sQuery(id+"F0.wireOp",EDGE,"E23.filletArc");var subQ11=sQuery(id+"F0.wireOp",EDGE,"E24.filletArc");Q0=makeQuery(id+"F2.boolean.opBoolean","SPLIT",FACE,{"disambiguationData":[TD([makeQuery(id+"F1.opExtrude","SWEPT_FACE",FACE,{"disambiguationData":[OSD([subQ5])]})])],"derivedFrom":makeQuery(id+"F1.opExtrude","CAP_FACE",FACE,{"disambiguationData":[OSD([subQ5,subQ7,subQ8,subQ9,subQ4,subQ3,subQ2,subQ1,subQ6,subQ0,subQ10,subQ11])],"isStart":true})});}
            var sketch = newSketch(context, id + "F16", { "sketchPlane" : qUnion([Q0])});
            skCircle(sketch, "E79", {"center": v(0, 104.25) * mm, "radius": 6 * mm});
            skLineSegment(sketch, "E80", {"start": v(-33, 74.25) * mm, "end": v(-15, 92.25) * mm});
            skLineSegment(sketch, "E81", {"start": v(33, 74.25) * mm, "end": v(15, 92.25) * mm});
            skLineSegment(sketch, "E82", {"start": v(-33, 74.25) * mm, "end": v(33, 74.25) * mm});
            skArc(sketch, "E83", {"start": v(-15, 104.25) * mm, "mid": v(0, 119.25) * mm, "end": v(15, 104.25) * mm});
            skLineSegment(sketch, "E84", {"start": v(-15, 104.25) * mm, "end": v(-15, 92.25) * mm});
            skLineSegment(sketch, "E85", {"start": v(15, 104.25) * mm, "end": v(15, 92.25) * mm});
            skLineSegment(sketch, "E86", {"start": v(0, 74.25) * mm, "end": v(0, 104.25) * mm, "construction": true});
            skLineSegment(sketch, "E87", {"start": v(0, 104.25) * mm, "end": v(-37.02, 104.25) * mm, "construction": true});
            skLineSegment(sketch, "E88", {"start": v(0, 104.25) * mm, "end": v(29.43, 104.25) * mm, "construction": true});
            skLineSegment(sketch, "E89", {"start": v(0, 0) * mm, "end": v(0, 159.4) * mm, "construction": true});
            skPoint(sketch, "E89.endSnap0", {"position": v(0, 119.25) * mm});
            skLineSegment(sketch, "E90", {"start": v(0, 0) * mm, "end": v(0, -130.65) * mm, "construction": true});
            skLineSegment(sketch, "E91", {"start": v(0, 0) * mm, "end": v(-126.51, 0) * mm, "construction": true});
            skPoint(sketch, "E91.endSnap0", {"position": v(-74.25, 0) * mm});
            skLineSegment(sketch, "E92", {"start": v(0, 0) * mm, "end": v(120.88, 0) * mm, "construction": true});
            skLineSegment(sketch, "E93", {"start": v(-64.25, 74.25) * mm, "end": v(64.25, 74.25) * mm});
            skLineSegment(sketch, "E94", {"start": v(74.25, 64.25) * mm, "end": v(74.25, -64.25) * mm});
            skLineSegment(sketch, "E95", {"start": v(-74.25, -64.25) * mm, "end": v(-74.25, 64.25) * mm});
            skCircle(sketch, "E96", {"center": v(-60, 60) * mm, "radius": 4 * mm});
            skArc(sketch, "E97", {"start": v(-64.25, 74.25) * mm, "mid": v(-71.32, 71.32) * mm, "end": v(-74.25, 64.25) * mm});
            skArc(sketch, "E98", {"start": v(74.25, 64.25) * mm, "mid": v(71.32, 71.32) * mm, "end": v(64.25, 74.25) * mm});
            skCircle(sketch, "E99", {"center": v(60, 60) * mm, "radius": 4 * mm});
            skLineSegment(sketch, "E100", {"start": v(-60, 0) * mm, "end": v(-60, 38.83) * mm});
            skArc(sketch, "E101", {"start": v(-54.26, 47.88) * mm, "mid": v(-58.44, 44.2) * mm, "end": v(-60, 38.83) * mm});
            skLineSegment(sketch, "E102", {"start": v(60, 0) * mm, "end": v(60, 38.83) * mm});
            skArc(sketch, "E103", {"start": v(60, 38.83) * mm, "mid": v(58.44, 44.2) * mm, "end": v(54.26, 47.88) * mm});
            skArc(sketch, "E104", {"start": v(54.26, 47.88) * mm, "mid": v(0, 59.99) * mm, "end": v(-54.26, 47.88) * mm});
            skArc(sketch, "E105.MirrorCS", {"start": v(-54.26, -47.88) * mm, "mid": v(-58.44, -44.2) * mm, "end": v(-60, -38.83) * mm});
            skArc(sketch, "E106.MirrorCS", {"start": v(60, -38.83) * mm, "mid": v(58.44, -44.2) * mm, "end": v(54.26, -47.88) * mm});
            skCircle(sketch, "E107.MirrorC", {"center": v(-60, -60) * mm, "radius": 4 * mm});
            skCircle(sketch, "E108.MirrorC", {"center": v(60, -60) * mm, "radius": 4 * mm});
            skLineSegment(sketch, "E109.MirrorCS", {"start": v(15, -104.25) * mm, "end": v(15, -92.25) * mm});
            skLineSegment(sketch, "E110.MirrorCS", {"start": v(-64.25, -74.25) * mm, "end": v(64.25, -74.25) * mm});
            skArc(sketch, "E111.MirrorCS", {"start": v(-64.25, -74.25) * mm, "mid": v(-71.32, -71.32) * mm, "end": v(-74.25, -64.25) * mm});
            skArc(sketch, "E112.MirrorCS", {"start": v(74.25, -64.25) * mm, "mid": v(71.32, -71.32) * mm, "end": v(64.25, -74.25) * mm});
            skLineSegment(sketch, "E113.MirrorCS", {"start": v(0, -74.25) * mm, "end": v(0, -104.25) * mm, "construction": true});
            skLineSegment(sketch, "E114.MirrorCS", {"start": v(33, -74.25) * mm, "end": v(15, -92.25) * mm});
            skLineSegment(sketch, "E115.MirrorCS", {"start": v(0, -104.25) * mm, "end": v(29.43, -104.25) * mm, "construction": true});
            skArc(sketch, "E116.MirrorCS", {"start": v(-15, -104.25) * mm, "mid": v(0, -119.25) * mm, "end": v(15, -104.25) * mm});
            skLineSegment(sketch, "E117.MirrorCS", {"start": v(-33, -74.25) * mm, "end": v(33, -74.25) * mm});
            skLineSegment(sketch, "E118.MirrorCS", {"start": v(-33, -74.25) * mm, "end": v(-15, -92.25) * mm});
            skCircle(sketch, "E119.MirrorC", {"center": v(0, -104.25) * mm, "radius": 6 * mm});
            skPoint(sketch, "E120.MirrorP", {"position": v(0, -119.25) * mm});
            skArc(sketch, "E121.MirrorCS", {"start": v(54.26, -47.88) * mm, "mid": v(0, -59.99) * mm, "end": v(-54.26, -47.88) * mm});
            skLineSegment(sketch, "E122.MirrorCS", {"start": v(0, -104.25) * mm, "end": v(-37.02, -104.25) * mm, "construction": true});
            skLineSegment(sketch, "E123.MirrorCS", {"start": v(-15, -104.25) * mm, "end": v(-15, -92.25) * mm});
            skLineSegment(sketch, "E124.MirrorCS", {"start": v(60, 0) * mm, "end": v(60, -38.83) * mm});
            skLineSegment(sketch, "E125.MirrorCS", {"start": v(-60, 0) * mm, "end": v(-60, -38.83) * mm});
            skSolve(sketch);
        }
        {
            var Q0;
            Q0 = qSketchRegion(id + "F16", true);
            var Q1;
            Q1=makeQuery(id+"F2.opExtrude","CAP_FACE",FACE,{"disambiguationData":[OSD([sQuery(id+"F0.wireOp",EDGE,"E12"),sQuery(id+"F0.wireOp",EDGE,"E13"),sQuery(id+"F0.wireOp",EDGE,"E14"),sQuery(id+"F0.wireOp",EDGE,"E15"),sQuery(id+"F0.wireOp",EDGE,"E17.filletArc"),sQuery(id+"F0.wireOp",EDGE,"E18.filletArc"),sQuery(id+"F0.wireOp",EDGE,"E19.filletArc"),sQuery(id+"F0.wireOp",EDGE,"E20.filletArc"),sQuery(id+"F0.wireOp",EDGE,"E25.0"),sQuery(id+"F0.wireOp",EDGE,"E25.1"),sQuery(id+"F0.wireOp",EDGE,"E25.2"),sQuery(id+"F0.wireOp",EDGE,"E25.3"),sQuery(id+"F0.wireOp",EDGE,"E25.4"),sQuery(id+"F0.wireOp",EDGE,"E25.5"),sQuery(id+"F0.wireOp",EDGE,"E25.6"),sQuery(id+"F0.wireOp",EDGE,"E25.7")])],"isStart":false});
            extrude(context, id + "F17", {"entities" : qUnion([Q0]), "operationType" : NewBodyOperationType.ADD, "endBound" : BoundingType.UP_TO_SURFACE, "endBoundEntityFace" : qUnion([Q1]), "depth" : 25 * mm});
        }
    });
